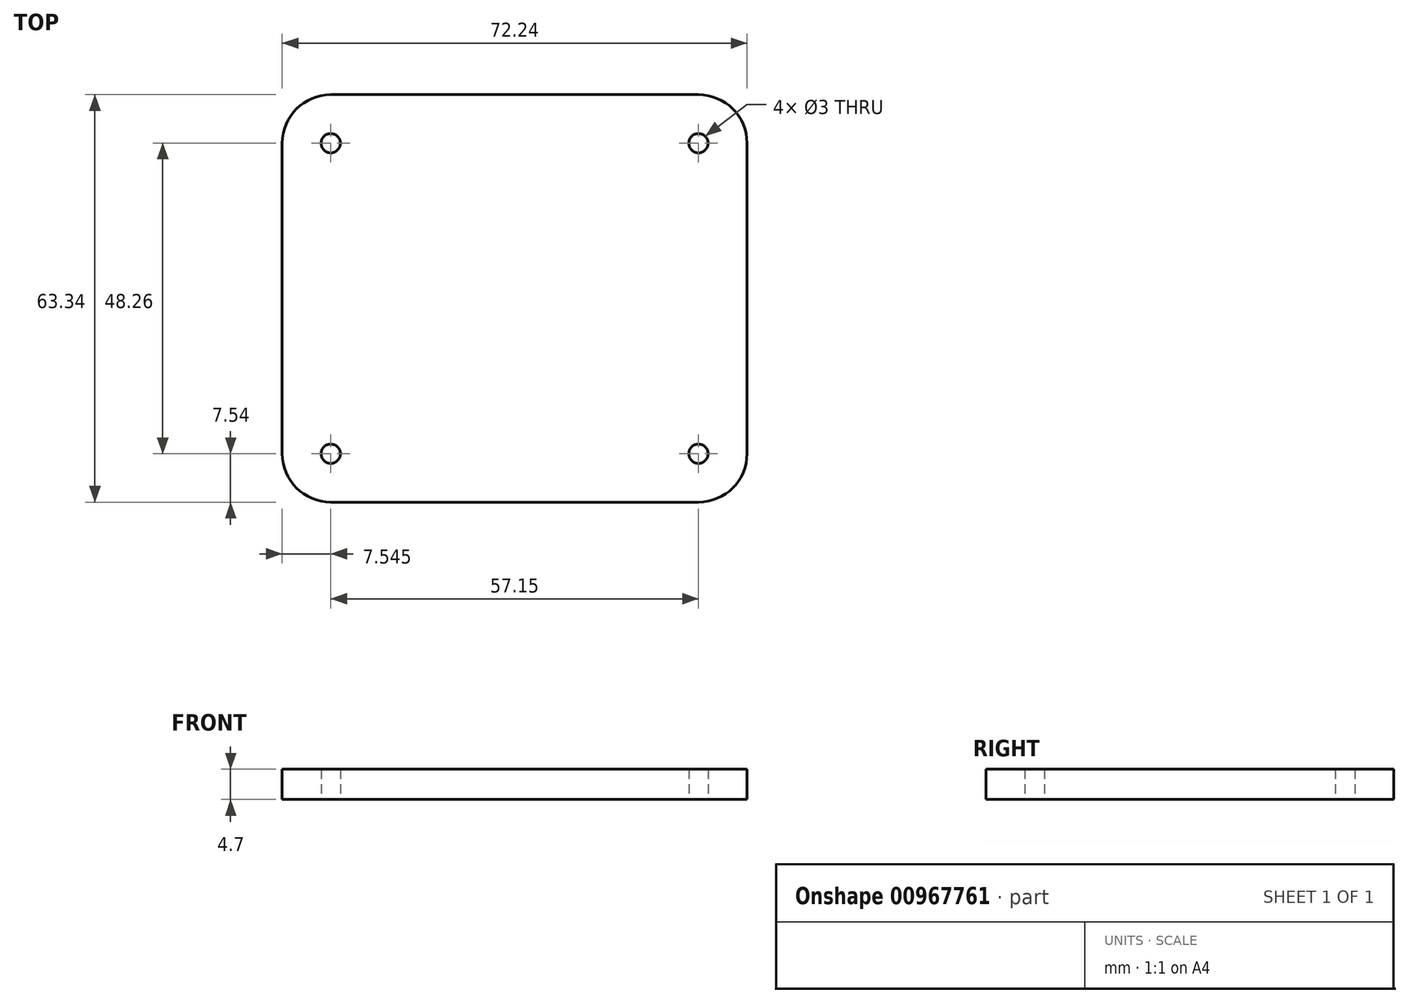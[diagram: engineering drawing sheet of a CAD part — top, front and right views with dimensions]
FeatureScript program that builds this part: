
annotation { "Feature Type Name" : "Feature", "Feature Type Description" : "" }
export const myFeature = defineFeature(function(context is Context, id is Id, definition is map)
    precondition{}
    {
        {
            var Q0;
            Q0=qCreatedBy(makeId("Top.planeOp"),FACE);
            var sketch = newSketch(context, id + "F0", { "sketchPlane" : qUnion([Q0])});
            skLineSegment(sketch, "E0.bottom", {"start": v(28.58, 31.67) * mm, "end": v(-28.57, 31.67) * mm});
            skLineSegment(sketch, "E0.top", {"start": v(28.58, -31.67) * mm, "end": v(-28.57, -31.67) * mm});
            skLineSegment(sketch, "E0.left", {"start": v(36.12, 24.13) * mm, "end": v(36.12, -24.13) * mm});
            skLineSegment(sketch, "E0.right", {"start": v(-36.11, 24.13) * mm, "end": v(-36.11, -24.13) * mm});
            skPoint(sketch, "E0.middle", {"position": v(0, 0) * mm});
            skPoint(sketch, "E1.visualSharp", {"position": v(-36.12, 31.67) * mm});
            skArc(sketch, "E1.filletArc", {"start": v(-28.57, 31.67) * mm, "mid": v(-33.9, 29.46) * mm, "end": v(-36.12, 24.13) * mm});
            skPoint(sketch, "E2.visualSharp", {"position": v(36.11, 31.67) * mm});
            skArc(sketch, "E2.filletArc", {"start": v(36.12, 24.13) * mm, "mid": v(33.9, 29.46) * mm, "end": v(28.58, 31.67) * mm});
            skPoint(sketch, "E3.visualSharp", {"position": v(36.11, -31.67) * mm});
            skArc(sketch, "E3.filletArc", {"start": v(28.58, -31.67) * mm, "mid": v(33.9, -29.46) * mm, "end": v(36.12, -24.13) * mm});
            skPoint(sketch, "E4.visualSharp", {"position": v(-36.11, -31.67) * mm});
            skArc(sketch, "E4.filletArc", {"start": v(-36.11, -24.13) * mm, "mid": v(-33.9, -29.46) * mm, "end": v(-28.57, -31.67) * mm});
            skCircle(sketch, "E5", {"center": v(-28.57, 24.13) * mm, "radius": 1.5 * mm});
            skLineSegment(sketch, "E6", {"start": v(0, 31.67) * mm, "end": v(0, -31.67) * mm, "construction": true});
            skLineSegment(sketch, "E7", {"start": v(-36.12, 0) * mm, "end": v(36.12, 0) * mm, "construction": true});
            skCircle(sketch, "E8.MirrorC", {"center": v(28.58, 24.13) * mm, "radius": 1.5 * mm});
            skCircle(sketch, "E9.MirrorC", {"center": v(28.58, -24.13) * mm, "radius": 1.5 * mm});
            skCircle(sketch, "E10.MirrorC", {"center": v(-28.57, -24.13) * mm, "radius": 1.5 * mm});
            skSolve(sketch);
        }
        {
            var Q0;
            Q0=makeQuery(id+"F0.imprint","IMPRINT",FACE,{"disambiguationData":[TD([[makeQuery(id+"F0.imprint","IMPRINT",EDGE,{"derivedFrom":sQuery(id+"F0.wireOp",EDGE,"E0.bottom")}),1.0]])]});
            extrude(context, id + "F1", {"entities" : qUnion([Q0]), "depth" : 4.7 * mm, "offsetDistance" : 25 * mm});
        }
    });
